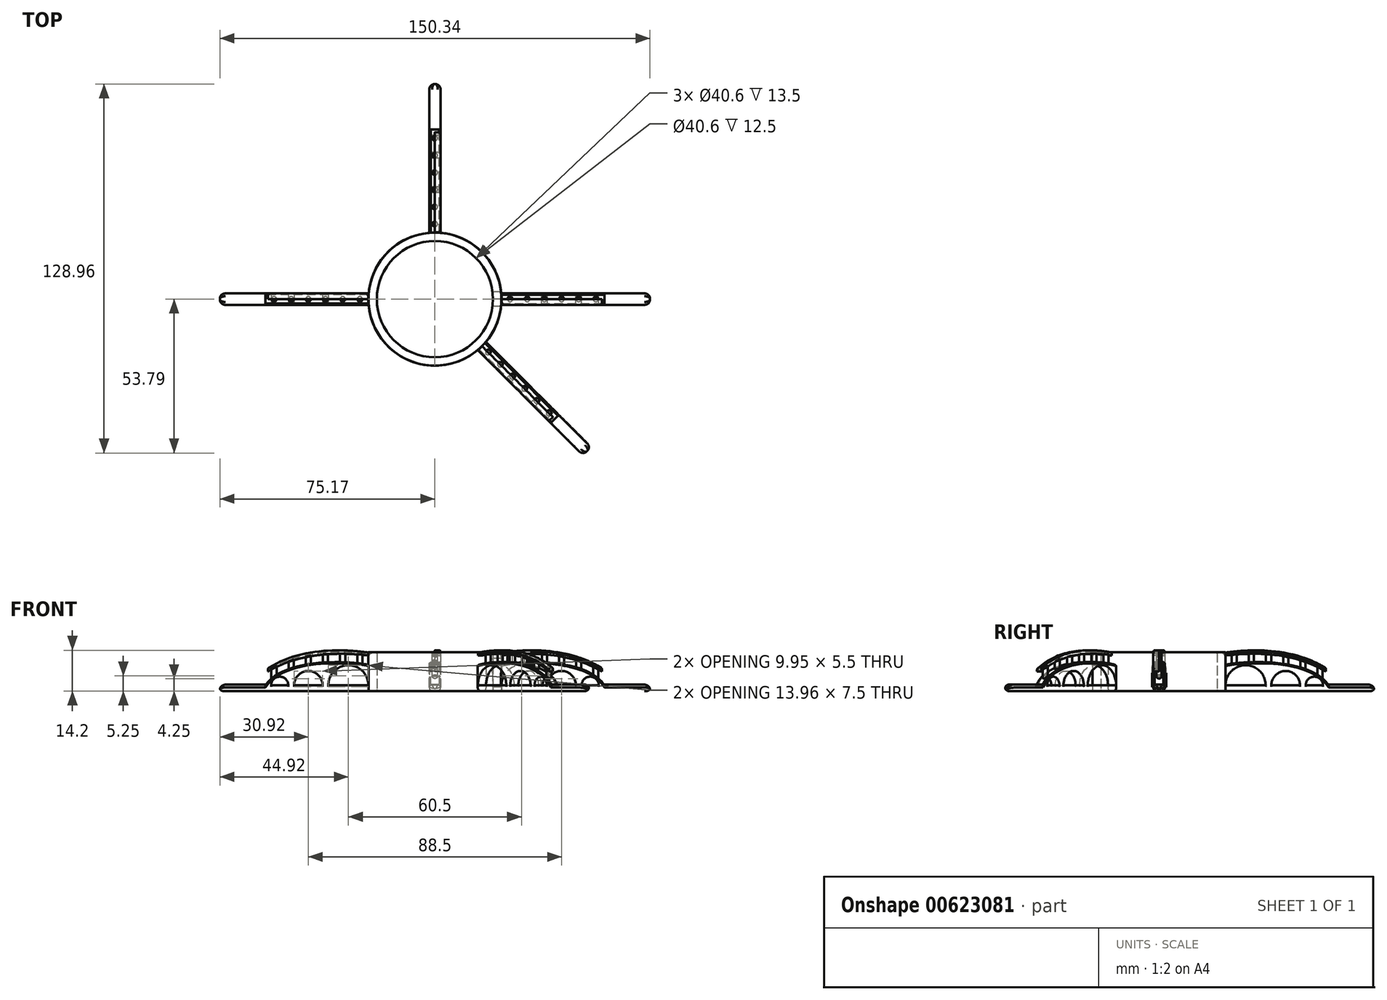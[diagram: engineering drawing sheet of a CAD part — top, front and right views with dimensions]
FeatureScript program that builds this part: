
annotation { "Feature Type Name" : "Feature", "Feature Type Description" : "" }
export const myFeature = defineFeature(function(context is Context, id is Id, definition is map)
    precondition{}
    {
        {
            var Q0;
            Q0=qCreatedBy(makeId("Top.planeOp"),FACE);
            var sketch = newSketch(context, id + "F0", { "sketchPlane" : qUnion([Q0])});
            skCircle(sketch, "E0", {"center": v(0, 0) * mm, "radius": 20.3 * mm});
            skCircle(sketch, "E1", {"center": v(0, 0) * mm, "radius": 23.25 * mm});
            skSolve(sketch);
        }
        {
            var Q0;
            Q0 = qSketchRegion(id + "F0", true);
            extrude(context, id + "F1", {"entities" : qUnion([Q0]), "depth" : 13.5 * mm, "offsetDistance" : 25 * mm});
        }
        {
            var Q0;
            Q0=qCreatedBy(makeId("Front.planeOp"),FACE);
            var sketch = newSketch(context, id + "F2", { "sketchPlane" : qUnion([Q0])});
            skLineSegment(sketch, "E2", {"start": v(0, 0) * mm, "end": v(23.25, 0) * mm});
            skLineSegment(sketch, "E3", {"start": v(23.25, 0) * mm, "end": v(23.25, 2) * mm});
            skLineSegment(sketch, "E4", {"start": v(23.25, 0) * mm, "end": v(16.87, 0) * mm});
            skLineSegment(sketch, "E5", {"start": v(59.25, 2) * mm, "end": v(23.25, 2) * mm});
            skPoint(sketch, "E6.start.orphan", {"position": v(16.87, 15) * mm});
            skLineSegment(sketch, "E7", {"start": v(23.25, 2) * mm, "end": v(23.25, 2) * mm});
            skLineSegment(sketch, "E8", {"start": v(23.25, 2) * mm, "end": v(23.25, 0) * mm});
            skLineSegment(sketch, "E9", {"start": v(23.25, 0) * mm, "end": v(23.25, 0) * mm});
            skLineSegment(sketch, "E10", {"start": v(23.25, 0) * mm, "end": v(59.25, 0) * mm});
            skArc(sketch, "E11", {"start": v(37.25, 2) * mm, "mid": v(30.25, 9) * mm, "end": v(23.25, 2) * mm});
            skLineSegment(sketch, "E12", {"start": v(37.25, 2) * mm, "end": v(39.25, 2) * mm});
            skLineSegment(sketch, "E13", {"start": v(39.25, 2) * mm, "end": v(39.25, 0) * mm});
            skArc(sketch, "E14", {"start": v(49.25, 2) * mm, "mid": v(44.25, 7) * mm, "end": v(39.25, 2) * mm});
            skLineSegment(sketch, "E15", {"start": v(49.25, 2) * mm, "end": v(51.25, 2) * mm});
            skLineSegment(sketch, "E16", {"start": v(51.25, 2) * mm, "end": v(51.25, 0) * mm});
            skArc(sketch, "E17", {"start": v(57.25, 2) * mm, "mid": v(54.25, 5) * mm, "end": v(51.25, 2) * mm});
            skLineSegment(sketch, "E18", {"start": v(57.25, 2) * mm, "end": v(59.25, 2) * mm});
            skLineSegment(sketch, "E19", {"start": v(23.25, 2) * mm, "end": v(21.25, 2) * mm});
            skLineSegment(sketch, "E20", {"start": v(21.25, 2) * mm, "end": v(21.25, 0) * mm});
            skLineSegment(sketch, "E21", {"start": v(59.25, 2) * mm, "end": v(59.25, 0) * mm});
            skFitSpline(sketch, "E22", {"points": [v(59.25, 2) * mm, v(22.94, 9.1) * mm], "startDerivative": vector(-19.37, 28.89) * mm, "endDerivative": vector(-21.33, -4.66) * mm});
            skLineSegment(sketch, "E23", {"start": v(22.94, 9.1) * mm, "end": v(21.25, 2) * mm});
            skLineSegment(sketch, "E24", {"start": v(59.25, 1.2) * mm, "end": v(59.25, 2) * mm});
            skSolve(sketch);
        }
        {
            var Q0;
            Q0 = qSketchRegion(id + "F2", true);
            extrude(context, id + "F3", {"entities" : qUnion([Q0]), "operationType" : NewBodyOperationType.ADD, "depth" : 4 * mm, "offsetDistance" : 25 * mm, "symmetric" : true});
        }
        {
            var Q0;
            Q0=makeQuery(id+"F1.opExtrude","CAP_FACE",FACE,{"disambiguationData":[OSD([sQuery(id+"F0.wireOp",EDGE,"E0"),sQuery(id+"F0.wireOp",EDGE,"E1")])],"isStart":false});
            var sketch = newSketch(context, id + "F4", { "sketchPlane" : qUnion([Q0])});
            skLineSegment(sketch, "E25", {"start": v(23.25, 0) * mm, "end": v(58.86, 0) * mm});
            skCircle(sketch, "E26", {"center": v(26.25, 0) * mm, "radius": 0.9 * mm});
            skLineSegment(sketch, "E27.direction1", {"start": v(26.25, 0) * mm, "end": v(32.25, 0) * mm, "construction": true});
            skCircle(sketch, "E28.1.0.0", {"center": v(32.25, 0) * mm, "radius": 0.9 * mm});
            skCircle(sketch, "E28.2.0.0", {"center": v(38.25, 0) * mm, "radius": 0.9 * mm});
            skCircle(sketch, "E28.3.0.0", {"center": v(44.25, 0) * mm, "radius": 0.9 * mm});
            skCircle(sketch, "E28.4.0.0", {"center": v(50.25, 0) * mm, "radius": 0.9 * mm});
            skCircle(sketch, "E28.5.0.0", {"center": v(56.25, 0) * mm, "radius": 0.9 * mm});
            skSolve(sketch);
        }
        {
            var Q0;
            Q0 = qSketchRegion(id + "F4", true);
            extrude(context, id + "F5", {"entities" : qUnion([Q0]), "operationType" : NewBodyOperationType.ADD, "endBound" : BoundingType.UP_TO_NEXT, "oppositeDirection" : true, "depth" : 25 * mm, "offsetDistance" : 25 * mm});
        }
        {
            var Q0;
            Q0=makeQuery(id+"F3.opExtrude","CAP_FACE",FACE,{"disambiguationData":[OSD([sQuery(id+"F2.wireOp",EDGE,"E4"),sQuery(id+"F2.wireOp",EDGE,"eUv9CqKa-Kuf0-0BP2-0XyY-XhsE2m74vfEs"),sQuery(id+"F2.wireOp",EDGE,"E5"),sQuery(id+"F2.wireOp",EDGE,"E10"),sQuery(id+"F2.wireOp",EDGE,"E11"),sQuery(id+"F2.wireOp",EDGE,"E14"),sQuery(id+"F2.wireOp",EDGE,"E17"),sQuery(id+"F2.wireOp",EDGE,"E5"),sQuery(id+"F2.wireOp",EDGE,"E20"),sQuery(id+"F2.wireOp",EDGE,"E22"),sQuery(id+"F2.wireOp",EDGE,"E23")])],"isStart":false});
            var sketch = newSketch(context, id + "F6", { "sketchPlane" : qUnion([Q0])});
            skFitSpline(sketch, "E29", {"points": [v(23.74, 12.54) * mm, v(61.85, 4.86) * mm], "startDerivative": vector(38.13, 4.2) * mm, "endDerivative": vector(33.52, -24.72) * mm});
            skLineSegment(sketch, "E30", {"start": v(23.74, 12.54) * mm, "end": v(23.74, 22.54) * mm});
            skLineSegment(sketch, "E31", {"start": v(61.85, 4.86) * mm, "end": v(61.85, 19.86) * mm});
            skFitSpline(sketch, "E32", {"points": [v(61.85, 19.86) * mm, v(23.74, 22.54) * mm], "startDerivative": vector(-32.68, 25.7) * mm, "endDerivative": vector(-38.13, -5.59) * mm});
            skSolve(sketch);
        }
        {
            var Q0;
            Q0 = qSketchRegion(id + "F6", true);
            extrude(context, id + "F7", {"entities" : qUnion([Q0]), "operationType" : NewBodyOperationType.REMOVE, "oppositeDirection" : true, "depth" : 7 * mm, "offsetDistance" : 25 * mm});
        }
        {
            var Q0;
            Q0=makeQuery(id+"F3.opExtrude","CAP_FACE",FACE,{"disambiguationData":[OSD([sQuery(id+"F2.wireOp",EDGE,"E4"),sQuery(id+"F2.wireOp",EDGE,"eUv9CqKa-Kuf0-0BP2-0XyY-XhsE2m74vfEs"),sQuery(id+"F2.wireOp",EDGE,"E5"),sQuery(id+"F2.wireOp",EDGE,"E10"),sQuery(id+"F2.wireOp",EDGE,"E11"),sQuery(id+"F2.wireOp",EDGE,"E14"),sQuery(id+"F2.wireOp",EDGE,"E17"),sQuery(id+"F2.wireOp",EDGE,"E5"),sQuery(id+"F2.wireOp",EDGE,"E20"),sQuery(id+"F2.wireOp",EDGE,"E22"),sQuery(id+"F2.wireOp",EDGE,"E23")])],"isStart":false});
            var sketch = newSketch(context, id + "F8", { "sketchPlane" : qUnion([Q0])});
            skFitSpline(sketch, "E33", {"points": [v(23.33, 12.44) * mm, v(61.44, 4.76) * mm], "startDerivative": vector(38.13, 4.2) * mm, "endDerivative": vector(33.52, -24.72) * mm});
            skLineSegment(sketch, "E34", {"start": v(23.33, 12.44) * mm, "end": v(23.33, 13.44) * mm});
            skFitSpline(sketch, "E35", {"points": [v(61.44, 5.76) * mm, v(23.33, 13.44) * mm], "startDerivative": vector(-33.52, 26.14) * mm, "endDerivative": vector(-38.16, -5.2) * mm});
            skLineSegment(sketch, "E36", {"start": v(58.3, 6.84) * mm, "end": v(58.3, 7.95) * mm});
            skSolve(sketch);
        }
        {
            var Q0;
            Q0 = qSketchRegion(id + "F8", true);
            extrude(context, id + "F9", {"entities" : qUnion([Q0]), "operationType" : NewBodyOperationType.ADD, "oppositeDirection" : true, "depth" : 2 * mm, "offsetDistance" : 25 * mm});
        }
        {
            var Q0;
            Q0=makeQuery(id+"F3.opExtrude","CAP_EDGE",EDGE,{"disambiguationData":[OSD([sQuery(id+"F2.wireOp",EDGE,"E22")])],"isStart":true});
            var Q1;
            Q1=makeQuery(id+"F3.opExtrude","CAP_EDGE",EDGE,{"disambiguationData":[OSD([sQuery(id+"F2.wireOp",EDGE,"E22")])],"isStart":false});
            chamfer(context, id + "F10", {"entities" : qUnion([Q0, Q1]), "chamferType" : ChamferType.OFFSET_ANGLE, "width" : 0.5 * mm, "oppositeDirection" : false, "angle" : 40 * degree, "tangentPropagation" : true});
        }
        {
            var Q0;
            {var subQ0=sQuery(id+"F2.wireOp",EDGE,"E5");var subQ1=sQuery(id+"F2.wireOp",EDGE,"E11");Q0=makeQuery(id+"F3.opExtrude","CAP_EDGE",EDGE,{"disambiguationData":[OSD([subQ0]),TDD([makeQuery(id+"F2.imprint","IMPRINT",EDGE,{"disambiguationData":[TD([[makeQuery(id+"F2.imprint","INTERSECT",VERTEX,{"derivedFrom":[subQ1,subQ0]}),-1.0]])],"derivedFrom":subQ0})])],"isStart":false});}
            var Q1;
            {var subQ0=sQuery(id+"F2.wireOp",EDGE,"E5");var subQ1=sQuery(id+"F2.wireOp",EDGE,"E14");Q1=makeQuery(id+"F3.opExtrude","CAP_EDGE",EDGE,{"disambiguationData":[OSD([subQ0]),TDD([makeQuery(id+"F2.imprint","IMPRINT",EDGE,{"disambiguationData":[TD([[makeQuery(id+"F2.imprint","INTERSECT",VERTEX,{"derivedFrom":[subQ1,subQ0]}),-1.0]])],"derivedFrom":subQ0})])],"isStart":false});}
            var Q2;
            {var subQ0=sQuery(id+"F2.wireOp",EDGE,"E5");var subQ1=sQuery(id+"F2.wireOp",EDGE,"E11");Q2=makeQuery(id+"F3.opExtrude","CAP_EDGE",EDGE,{"disambiguationData":[OSD([subQ0]),TDD([makeQuery(id+"F2.imprint","IMPRINT",EDGE,{"disambiguationData":[TD([[makeQuery(id+"F2.imprint","INTERSECT",VERTEX,{"derivedFrom":[subQ1,subQ0]}),-1.0]])],"derivedFrom":subQ0})])],"isStart":true});}
            var Q3;
            {var subQ0=sQuery(id+"F2.wireOp",EDGE,"E5");var subQ1=sQuery(id+"F2.wireOp",EDGE,"E14");Q3=makeQuery(id+"F3.opExtrude","CAP_EDGE",EDGE,{"disambiguationData":[OSD([subQ0]),TDD([makeQuery(id+"F2.imprint","IMPRINT",EDGE,{"disambiguationData":[TD([[makeQuery(id+"F2.imprint","INTERSECT",VERTEX,{"derivedFrom":[subQ1,subQ0]}),-1.0]])],"derivedFrom":subQ0})])],"isStart":true});}
            var Q4;
            {var subQ0=sQuery(id+"F2.wireOp",EDGE,"E5");var subQ1=sQuery(id+"F2.wireOp",EDGE,"E17");Q4=makeQuery(id+"F3.opExtrude","CAP_EDGE",EDGE,{"disambiguationData":[OSD([subQ0]),TDD([makeQuery(id+"F2.imprint","IMPRINT",EDGE,{"disambiguationData":[TD([[makeQuery(id+"F2.imprint","INTERSECT",VERTEX,{"derivedFrom":[subQ1,subQ0]}),-1.0]])],"derivedFrom":subQ0})])],"isStart":true});}
            var Q5;
            {var subQ0=sQuery(id+"F2.wireOp",EDGE,"E5");var subQ1=sQuery(id+"F2.wireOp",EDGE,"E17");Q5=makeQuery(id+"F3.opExtrude","CAP_EDGE",EDGE,{"disambiguationData":[OSD([subQ0]),TDD([makeQuery(id+"F2.imprint","IMPRINT",EDGE,{"disambiguationData":[TD([[makeQuery(id+"F2.imprint","INTERSECT",VERTEX,{"derivedFrom":[subQ1,subQ0]}),-1.0]])],"derivedFrom":subQ0})])],"isStart":false});}
            var Q6;
            Q6=makeQuery(id+"FbmkzwlNqpSPATz_1.1.F9.opExtrude","CAP_EDGE",EDGE,{"disambiguationData":[OSD([sQuery(id+"F8.wireOp",EDGE,"E35")])],"isStart":true});
            var Q7;
            Q7=makeQuery(id+"F9.opExtrude","CAP_EDGE",EDGE,{"disambiguationData":[OSD([sQuery(id+"F8.wireOp",EDGE,"E35")])],"isStart":true});
            var Q8;
            {var subQ0=sQuery(id+"F8.wireOp",EDGE,"E35");var subQ1=sQuery(id+"F8.wireOp",EDGE,"bGR884Nu-NAzO-R1rn-mJv8-BLiTySfXEnIB");Q8=makeQuery(id+"FbmkzwlNqpSPATz_1.1.F9.boolean.opBoolean","MERGE",EDGE,{"derivedFrom":[makeQuery(id+"F9.opExtrude","SWEPT_EDGE",EDGE,{"disambiguationData":[OSD([subQ1,subQ0])]}),makeQuery(id+"FbmkzwlNqpSPATz_1.1.F9.opExtrude","SWEPT_EDGE",EDGE,{"disambiguationData":[OSD([subQ1,subQ0])]})]});}
            fillet(context, id + "F11", {"entities" : qUnion([Q0, Q1, Q2, Q3, Q4, Q5, Q6, Q7, Q8]), "radius" : 0.5 * mm, "tangentPropagation" : true, "allowEdgeOverflow" : false});
        }
        {
            var Q0;
            Q0=makeQuery(id+"F3.opExtrude","CAP_FACE",FACE,{"disambiguationData":[OSD([sQuery(id+"F2.wireOp",EDGE,"E4"),sQuery(id+"F2.wireOp",EDGE,"E10"),sQuery(id+"F2.wireOp",EDGE,"E11"),sQuery(id+"F2.wireOp",EDGE,"E14"),sQuery(id+"F2.wireOp",EDGE,"E17"),sQuery(id+"F2.wireOp",EDGE,"E5"),sQuery(id+"F2.wireOp",EDGE,"E20"),sQuery(id+"F2.wireOp",EDGE,"E21"),sQuery(id+"F2.wireOp",EDGE,"E22"),sQuery(id+"F2.wireOp",EDGE,"E23"),sQuery(id+"F2.wireOp",EDGE,"E24")])],"isStart":true});
            var sketch = newSketch(context, id + "F12", { "sketchPlane" : qUnion([Q0])});
            skLineSegment(sketch, "E37", {"start": v(-59.25, 0) * mm, "end": v(-75.25, 0) * mm});
            skLineSegment(sketch, "E38", {"start": v(-75.25, 0) * mm, "end": v(-75.25, 2.2) * mm});
            skLineSegment(sketch, "E39", {"start": v(-75.25, 2.2) * mm, "end": v(-59.25, 2.2) * mm});
            skLineSegment(sketch, "E40", {"start": v(-59.25, 2.2) * mm, "end": v(-59.25, 0) * mm});
            skSolve(sketch);
        }
        {
            var Q0;
            Q0 = qSketchRegion(id + "F12", true);
            extrude(context, id + "F13", {"entities" : qUnion([Q0]), "operationType" : NewBodyOperationType.ADD, "oppositeDirection" : true, "depth" : 4 * mm, "offsetDistance" : 25 * mm});
        }
        {
            var Q0;
            Q0=makeQuery(id+"F13.opExtrude","CAP_EDGE",EDGE,{"disambiguationData":[OSD([sQuery(id+"F12.wireOp",EDGE,"E39")])],"isStart":true});
            var Q1;
            Q1=makeQuery(id+"F13.opExtrude","CAP_EDGE",EDGE,{"disambiguationData":[OSD([sQuery(id+"F12.wireOp",EDGE,"E39")])],"isStart":false});
            fillet(context, id + "F14", {"entities" : qUnion([Q0, Q1]), "radius" : 1 * mm, "tangentPropagation" : true, "allowEdgeOverflow" : false});
        }
        {
            var Q0;
            Q0=makeQuery(id+"F14.opFillet","BLEND_EDGE",EDGE,{"blendedFrom":[makeQuery(id+"F13.opExtrude","CAP_EDGE",EDGE,{"disambiguationData":[OSD([sQuery(id+"F12.wireOp",EDGE,"E39")])],"isStart":true}),makeQuery(id+"F13.opExtrude","SWEPT_FACE",FACE,{"disambiguationData":[OSD([sQuery(id+"F12.wireOp",EDGE,"E38")])]})],"blendedInto":[makeQuery(id+"F13.opExtrude","SWEPT_FACE",FACE,{"disambiguationData":[OSD([sQuery(id+"F12.wireOp",EDGE,"E38")])]})]});
            fillet(context, id + "F15", {"entities" : qUnion([Q0]), "radius" : 2 * mm, "tangentPropagation" : true, "allowEdgeOverflow" : false});
        }
        {
            var Q0;
            Q0=makeQuery(id+"F1.opExtrude","SWEPT_BODY",BODY,{"disambiguationData":[OSD([sQuery(id+"F0.wireOp",EDGE,"E0"),sQuery(id+"F0.wireOp",EDGE,"E1")])]});
            var Q1;
            Q1=makeQuery(id+"F1.opExtrude","CAP_EDGE",EDGE,{"disambiguationData":[OSD([sQuery(id+"F0.wireOp",EDGE,"E1")])],"isStart":false});
            circularPattern(context, id + "F16", {"entities" : qUnion([Q0]), "axis" : qUnion([Q1]), "angle" : 360 * degree, "instanceCount" : 4, "equalSpace" : true});
        }
        {
            var Q0;
            Q0=qCreatedBy(makeId("Right.planeOp"),FACE);
            var sketch = newSketch(context, id + "F17", { "sketchPlane" : qUnion([Q0])});
            skLineSegment(sketch, "E41.bottom", {"start": v(2.5, 6.34) * mm, "end": v(-2.5, 6.34) * mm});
            skLineSegment(sketch, "E41.top", {"start": v(2.5, 1.34) * mm, "end": v(-2.5, 1.34) * mm});
            skLineSegment(sketch, "E41.left", {"start": v(2.5, 6.34) * mm, "end": v(2.5, 1.34) * mm});
            skLineSegment(sketch, "E41.right", {"start": v(-2.5, 6.34) * mm, "end": v(-2.5, 1.34) * mm});
            skPoint(sketch, "E41.middle", {"position": v(0, 3.84) * mm});
            skPoint(sketch, "E42.1.internal.snap0", {"position": v(0, 6.34) * mm});
            skFitSpline(sketch, "E42", {"points": [v(-2.5, 6.34) * mm, v(0, 11.34) * mm], "startDerivative": vector(0, 6.14) * mm, "endDerivative": vector(7.5, 3.82) * mm});
            skFitSpline(sketch, "E43", {"points": [v(2.5, 6.34) * mm, v(0, 11.34) * mm], "startDerivative": vector(0, 6.14) * mm, "endDerivative": vector(-7.5, 3.82) * mm});
            skSolve(sketch);
        }
        {
            var Q0;
            Q0=makeQuery(id+"F17.imprint","IMPRINT",FACE,{"disambiguationData":[TD([[makeQuery(id+"F17.imprint","IMPRINT",EDGE,{"derivedFrom":sQuery(id+"F17.wireOp",EDGE,"E41.bottom")}),1.0]])]});
            var Q1;
            Q1=makeQuery(id+"F17.imprint","IMPRINT",FACE,{"disambiguationData":[TD([[makeQuery(id+"F17.imprint","IMPRINT",EDGE,{"derivedFrom":sQuery(id+"F17.wireOp",EDGE,"E41.bottom")}),-1.0]])]});
            var Q2;
            Q2=makeQuery(id+"F16.opPattern","COPY",FACE,{"derivedFrom":makeQuery(id+"F1.opExtrude","SWEPT_FACE",FACE,{"disambiguationData":[OSD([sQuery(id+"F0.wireOp",EDGE,"E1")])]}),"instanceName":"1"});
            extrude(context, id + "F18", {"entities" : qUnion([Q0, Q1]), "depth" : 25 * mm, "endBoundEntityFace" : qUnion([Q2]), "offsetDistance" : 25 * mm});
        }
        {
            var Q0;
            Q0=makeQuery(id+"F16.opPattern","COPY",BODY,{"derivedFrom":makeQuery(id+"F1.opExtrude","SWEPT_BODY",BODY,{"disambiguationData":[OSD([sQuery(id+"F0.wireOp",EDGE,"E0"),sQuery(id+"F0.wireOp",EDGE,"E1")])]}),"instanceName":"3"});
            var Q1;
            Q1=makeQuery(id+"F16.opPattern","COPY",EDGE,{"derivedFrom":makeQuery(id+"F1.opExtrude","CAP_EDGE",EDGE,{"disambiguationData":[OSD([sQuery(id+"F0.wireOp",EDGE,"E1")])],"isStart":false}),"instanceName":"3"});
            transform(context, id + "F19", {"entities" : qUnion([Q0]), "transformType" : TransformType.ROTATION, "transformAxis" : qUnion([Q1]), "angle" : 45 * degree, "makeCopy" : false});
        }
        {
            var Q0;
            Q0=makeQuery(id+"F18.opExtrude","SWEPT_BODY",BODY,{"disambiguationData":[OSD([sQuery(id+"F17.wireOp",EDGE,"E41.top"),sQuery(id+"F17.wireOp",EDGE,"E41.left"),sQuery(id+"F17.wireOp",EDGE,"E41.right"),sQuery(id+"F17.wireOp",EDGE,"E42"),sQuery(id+"F17.wireOp",EDGE,"E43")])]});
            var Q1;
            Q1=makeQuery(id+"FSJmOjyLK6ZuT0z_1.-11.F18.opExtrude","SWEPT_BODY",BODY,{"disambiguationData":[OSD([sQuery(id+"F17.wireOp",EDGE,"E41.top"),sQuery(id+"F17.wireOp",EDGE,"E41.left"),sQuery(id+"F17.wireOp",EDGE,"E41.right"),sQuery(id+"F17.wireOp",EDGE,"E42"),sQuery(id+"F17.wireOp",EDGE,"E43")])]});
            var Q2;
            Q2=makeQuery(id+"FSJmOjyLK6ZuT0z_1.-10.F18.opExtrude","SWEPT_BODY",BODY,{"disambiguationData":[OSD([sQuery(id+"F17.wireOp",EDGE,"E41.top"),sQuery(id+"F17.wireOp",EDGE,"E41.left"),sQuery(id+"F17.wireOp",EDGE,"E41.right"),sQuery(id+"F17.wireOp",EDGE,"E42"),sQuery(id+"F17.wireOp",EDGE,"E43")])]});
            var Q3;
            Q3=makeQuery(id+"FSJmOjyLK6ZuT0z_1.-9.F18.opExtrude","SWEPT_BODY",BODY,{"disambiguationData":[OSD([sQuery(id+"F17.wireOp",EDGE,"E41.top"),sQuery(id+"F17.wireOp",EDGE,"E41.left"),sQuery(id+"F17.wireOp",EDGE,"E41.right"),sQuery(id+"F17.wireOp",EDGE,"E42"),sQuery(id+"F17.wireOp",EDGE,"E43")])]});
            var Q4;
            Q4=makeQuery(id+"FSJmOjyLK6ZuT0z_1.-8.F18.opExtrude","SWEPT_BODY",BODY,{"disambiguationData":[OSD([sQuery(id+"F17.wireOp",EDGE,"E41.top"),sQuery(id+"F17.wireOp",EDGE,"E41.left"),sQuery(id+"F17.wireOp",EDGE,"E41.right"),sQuery(id+"F17.wireOp",EDGE,"E42"),sQuery(id+"F17.wireOp",EDGE,"E43")])]});
            var Q5;
            Q5=makeQuery(id+"FSJmOjyLK6ZuT0z_1.-7.F18.opExtrude","SWEPT_BODY",BODY,{"disambiguationData":[OSD([sQuery(id+"F17.wireOp",EDGE,"E41.top"),sQuery(id+"F17.wireOp",EDGE,"E41.left"),sQuery(id+"F17.wireOp",EDGE,"E41.right"),sQuery(id+"F17.wireOp",EDGE,"E42"),sQuery(id+"F17.wireOp",EDGE,"E43")])]});
            var Q6;
            Q6=makeQuery(id+"FSJmOjyLK6ZuT0z_1.-6.F18.opExtrude","SWEPT_BODY",BODY,{"disambiguationData":[OSD([sQuery(id+"F17.wireOp",EDGE,"E41.top"),sQuery(id+"F17.wireOp",EDGE,"E41.left"),sQuery(id+"F17.wireOp",EDGE,"E41.right"),sQuery(id+"F17.wireOp",EDGE,"E42"),sQuery(id+"F17.wireOp",EDGE,"E43")])]});
            var Q7;
            Q7=makeQuery(id+"FSJmOjyLK6ZuT0z_1.-5.F18.opExtrude","SWEPT_BODY",BODY,{"disambiguationData":[OSD([sQuery(id+"F17.wireOp",EDGE,"E41.top"),sQuery(id+"F17.wireOp",EDGE,"E41.left"),sQuery(id+"F17.wireOp",EDGE,"E41.right"),sQuery(id+"F17.wireOp",EDGE,"E42"),sQuery(id+"F17.wireOp",EDGE,"E43")])]});
            var Q8;
            Q8=makeQuery(id+"FSJmOjyLK6ZuT0z_1.-4.F18.opExtrude","SWEPT_BODY",BODY,{"disambiguationData":[OSD([sQuery(id+"F17.wireOp",EDGE,"E41.top"),sQuery(id+"F17.wireOp",EDGE,"E41.left"),sQuery(id+"F17.wireOp",EDGE,"E41.right"),sQuery(id+"F17.wireOp",EDGE,"E42"),sQuery(id+"F17.wireOp",EDGE,"E43")])]});
            var Q9;
            Q9=makeQuery(id+"FSJmOjyLK6ZuT0z_1.-3.F18.opExtrude","SWEPT_BODY",BODY,{"disambiguationData":[OSD([sQuery(id+"F17.wireOp",EDGE,"E41.top"),sQuery(id+"F17.wireOp",EDGE,"E41.left"),sQuery(id+"F17.wireOp",EDGE,"E41.right"),sQuery(id+"F17.wireOp",EDGE,"E42"),sQuery(id+"F17.wireOp",EDGE,"E43")])]});
            var Q10;
            Q10=makeQuery(id+"FSJmOjyLK6ZuT0z_1.-2.F18.opExtrude","SWEPT_BODY",BODY,{"disambiguationData":[OSD([sQuery(id+"F17.wireOp",EDGE,"E41.top"),sQuery(id+"F17.wireOp",EDGE,"E41.left"),sQuery(id+"F17.wireOp",EDGE,"E41.right"),sQuery(id+"F17.wireOp",EDGE,"E42"),sQuery(id+"F17.wireOp",EDGE,"E43")])]});
            var Q11;
            Q11=makeQuery(id+"FSJmOjyLK6ZuT0z_1.-1.F18.opExtrude","SWEPT_BODY",BODY,{"disambiguationData":[OSD([sQuery(id+"F17.wireOp",EDGE,"E41.top"),sQuery(id+"F17.wireOp",EDGE,"E41.left"),sQuery(id+"F17.wireOp",EDGE,"E41.right"),sQuery(id+"F17.wireOp",EDGE,"E42"),sQuery(id+"F17.wireOp",EDGE,"E43")])]});
            var Q12;
            Q12=makeQuery(id+"FSJmOjyLK6ZuT0z_1.1.F18.opExtrude","SWEPT_BODY",BODY,{"disambiguationData":[OSD([sQuery(id+"F17.wireOp",EDGE,"E41.top"),sQuery(id+"F17.wireOp",EDGE,"E41.left"),sQuery(id+"F17.wireOp",EDGE,"E41.right"),sQuery(id+"F17.wireOp",EDGE,"E42"),sQuery(id+"F17.wireOp",EDGE,"E43")])]});
            var Q13;
            Q13=makeQuery(id+"FSJmOjyLK6ZuT0z_1.2.F18.opExtrude","SWEPT_BODY",BODY,{"disambiguationData":[OSD([sQuery(id+"F17.wireOp",EDGE,"E41.top"),sQuery(id+"F17.wireOp",EDGE,"E41.left"),sQuery(id+"F17.wireOp",EDGE,"E41.right"),sQuery(id+"F17.wireOp",EDGE,"E42"),sQuery(id+"F17.wireOp",EDGE,"E43")])]});
            var Q14;
            Q14=makeQuery(id+"FSJmOjyLK6ZuT0z_1.3.F18.opExtrude","SWEPT_BODY",BODY,{"disambiguationData":[OSD([sQuery(id+"F17.wireOp",EDGE,"E41.top"),sQuery(id+"F17.wireOp",EDGE,"E41.left"),sQuery(id+"F17.wireOp",EDGE,"E41.right"),sQuery(id+"F17.wireOp",EDGE,"E42"),sQuery(id+"F17.wireOp",EDGE,"E43")])]});
            var Q15;
            Q15=makeQuery(id+"FSJmOjyLK6ZuT0z_1.4.F18.opExtrude","SWEPT_BODY",BODY,{"disambiguationData":[OSD([sQuery(id+"F17.wireOp",EDGE,"E41.top"),sQuery(id+"F17.wireOp",EDGE,"E41.left"),sQuery(id+"F17.wireOp",EDGE,"E41.right"),sQuery(id+"F17.wireOp",EDGE,"E42"),sQuery(id+"F17.wireOp",EDGE,"E43")])]});
            var Q16;
            Q16=makeQuery(id+"FSJmOjyLK6ZuT0z_1.5.F18.opExtrude","SWEPT_BODY",BODY,{"disambiguationData":[OSD([sQuery(id+"F17.wireOp",EDGE,"E41.top"),sQuery(id+"F17.wireOp",EDGE,"E41.left"),sQuery(id+"F17.wireOp",EDGE,"E41.right"),sQuery(id+"F17.wireOp",EDGE,"E42"),sQuery(id+"F17.wireOp",EDGE,"E43")])]});
            var Q17;
            Q17=makeQuery(id+"FSJmOjyLK6ZuT0z_1.6.F18.opExtrude","SWEPT_BODY",BODY,{"disambiguationData":[OSD([sQuery(id+"F17.wireOp",EDGE,"E41.top"),sQuery(id+"F17.wireOp",EDGE,"E41.left"),sQuery(id+"F17.wireOp",EDGE,"E41.right"),sQuery(id+"F17.wireOp",EDGE,"E42"),sQuery(id+"F17.wireOp",EDGE,"E43")])]});
            var Q18;
            Q18=makeQuery(id+"FSJmOjyLK6ZuT0z_1.7.F18.opExtrude","SWEPT_BODY",BODY,{"disambiguationData":[OSD([sQuery(id+"F17.wireOp",EDGE,"E41.top"),sQuery(id+"F17.wireOp",EDGE,"E41.left"),sQuery(id+"F17.wireOp",EDGE,"E41.right"),sQuery(id+"F17.wireOp",EDGE,"E42"),sQuery(id+"F17.wireOp",EDGE,"E43")])]});
            var Q19;
            Q19=makeQuery(id+"FSJmOjyLK6ZuT0z_1.8.F18.opExtrude","SWEPT_BODY",BODY,{"disambiguationData":[OSD([sQuery(id+"F17.wireOp",EDGE,"E41.top"),sQuery(id+"F17.wireOp",EDGE,"E41.left"),sQuery(id+"F17.wireOp",EDGE,"E41.right"),sQuery(id+"F17.wireOp",EDGE,"E42"),sQuery(id+"F17.wireOp",EDGE,"E43")])]});
            var Q20;
            Q20=makeQuery(id+"FSJmOjyLK6ZuT0z_1.9.F18.opExtrude","SWEPT_BODY",BODY,{"disambiguationData":[OSD([sQuery(id+"F17.wireOp",EDGE,"E41.top"),sQuery(id+"F17.wireOp",EDGE,"E41.left"),sQuery(id+"F17.wireOp",EDGE,"E41.right"),sQuery(id+"F17.wireOp",EDGE,"E42"),sQuery(id+"F17.wireOp",EDGE,"E43")])]});
            var Q21;
            Q21=makeQuery(id+"FSJmOjyLK6ZuT0z_1.10.F18.opExtrude","SWEPT_BODY",BODY,{"disambiguationData":[OSD([sQuery(id+"F17.wireOp",EDGE,"E41.top"),sQuery(id+"F17.wireOp",EDGE,"E41.left"),sQuery(id+"F17.wireOp",EDGE,"E41.right"),sQuery(id+"F17.wireOp",EDGE,"E42"),sQuery(id+"F17.wireOp",EDGE,"E43")])]});
            var Q22;
            Q22=makeQuery(id+"FSJmOjyLK6ZuT0z_1.11.F18.opExtrude","SWEPT_BODY",BODY,{"disambiguationData":[OSD([sQuery(id+"F17.wireOp",EDGE,"E41.top"),sQuery(id+"F17.wireOp",EDGE,"E41.left"),sQuery(id+"F17.wireOp",EDGE,"E41.right"),sQuery(id+"F17.wireOp",EDGE,"E42"),sQuery(id+"F17.wireOp",EDGE,"E43")])]});
            var Q23;
            Q23=makeQuery(id+"F16.opPattern","COPY",BODY,{"derivedFrom":makeQuery(id+"F1.opExtrude","SWEPT_BODY",BODY,{"disambiguationData":[OSD([sQuery(id+"F0.wireOp",EDGE,"E0"),sQuery(id+"F0.wireOp",EDGE,"E1")])]}),"instanceName":"3"});
            booleanBodies(context, id + "F20", {"operationType" : BooleanOperationType.SUBTRACTION, "tools" : qUnion([Q0, Q1, Q2, Q3, Q4, Q5, Q6, Q7, Q8, Q9, Q10, Q11, Q12, Q13, Q14, Q15, Q16, Q17, Q18, Q19, Q20, Q21, Q22]), "targets" : qUnion([Q23])});
        }
        {
            var Q0;
            Q0=makeQuery(id+"F16.opPattern","COPY",EDGE,{"derivedFrom":makeQuery(id+"F1.opExtrude","CAP_EDGE",EDGE,{"disambiguationData":[OSD([sQuery(id+"F0.wireOp",EDGE,"E1")])],"isStart":false}),"instanceName":"3"});
            fillet(context, id + "F21", {"entities" : qUnion([Q0]), "radius" : 2 * mm, "tangentPropagation" : true, "allowEdgeOverflow" : false});
        }
        {
            var Q0;
            Q0=makeQuery(id+"F16.opPattern","COPY",EDGE,{"derivedFrom":makeQuery(id+"F1.opExtrude","CAP_EDGE",EDGE,{"disambiguationData":[OSD([sQuery(id+"F0.wireOp",EDGE,"E0")])],"isStart":false}),"instanceName":"3"});
            var Q1;
            Q1=makeQuery(id+"F16.opPattern","COPY",EDGE,{"derivedFrom":makeQuery(id+"F1.opExtrude","CAP_EDGE",EDGE,{"disambiguationData":[OSD([sQuery(id+"F0.wireOp",EDGE,"E0")])],"isStart":true}),"instanceName":"3"});
            fillet(context, id + "F22", {"entities" : qUnion([Q0, Q1]), "radius" : 0.5 * mm, "tangentPropagation" : true, "allowEdgeOverflow" : false});
        }
        {
            var Q0;
            Q0=makeQuery(id+"F16.opPattern","COPY",EDGE,{"derivedFrom":makeQuery(id+"F13.boolean.opBoolean","MERGE",EDGE,{"derivedFrom":[makeQuery(id+"F3.opExtrude","CAP_EDGE",EDGE,{"disambiguationData":[OSD([sQuery(id+"F2.wireOp",EDGE,"E4"),sQuery(id+"F2.wireOp",EDGE,"E10")])],"isStart":false}),makeQuery(id+"F13.opExtrude","CAP_EDGE",EDGE,{"disambiguationData":[OSD([sQuery(id+"F12.wireOp",EDGE,"E37")])],"isStart":false})]}),"instanceName":"1"});
            var Q1;
            Q1=makeQuery(id+"F16.opPattern","COPY",EDGE,{"derivedFrom":makeQuery(id+"F13.boolean.opBoolean","MERGE",EDGE,{"derivedFrom":[makeQuery(id+"F3.opExtrude","CAP_EDGE",EDGE,{"disambiguationData":[OSD([sQuery(id+"F2.wireOp",EDGE,"E4"),sQuery(id+"F2.wireOp",EDGE,"E10")])],"isStart":true}),makeQuery(id+"F13.opExtrude","CAP_EDGE",EDGE,{"disambiguationData":[OSD([sQuery(id+"F12.wireOp",EDGE,"E37")])],"isStart":true})]}),"instanceName":"1"});
            var Q2;
            Q2=makeQuery(id+"F16.opPattern","COPY",EDGE,{"derivedFrom":makeQuery(id+"F13.boolean.opBoolean","MERGE",EDGE,{"derivedFrom":[makeQuery(id+"F3.opExtrude","CAP_EDGE",EDGE,{"disambiguationData":[OSD([sQuery(id+"F2.wireOp",EDGE,"E4"),sQuery(id+"F2.wireOp",EDGE,"E10")])],"isStart":false}),makeQuery(id+"F13.opExtrude","CAP_EDGE",EDGE,{"disambiguationData":[OSD([sQuery(id+"F12.wireOp",EDGE,"E37")])],"isStart":false})]}),"instanceName":"2"});
            var Q3;
            Q3=makeQuery(id+"F16.opPattern","COPY",EDGE,{"derivedFrom":makeQuery(id+"F13.boolean.opBoolean","MERGE",EDGE,{"derivedFrom":[makeQuery(id+"F3.opExtrude","CAP_EDGE",EDGE,{"disambiguationData":[OSD([sQuery(id+"F2.wireOp",EDGE,"E4"),sQuery(id+"F2.wireOp",EDGE,"E10")])],"isStart":true}),makeQuery(id+"F13.opExtrude","CAP_EDGE",EDGE,{"disambiguationData":[OSD([sQuery(id+"F12.wireOp",EDGE,"E37")])],"isStart":true})]}),"instanceName":"2"});
            var Q4;
            Q4=makeQuery(id+"F16.opPattern","COPY",EDGE,{"derivedFrom":makeQuery(id+"F13.boolean.opBoolean","MERGE",EDGE,{"derivedFrom":[makeQuery(id+"F3.opExtrude","CAP_EDGE",EDGE,{"disambiguationData":[OSD([sQuery(id+"F2.wireOp",EDGE,"E4"),sQuery(id+"F2.wireOp",EDGE,"E10")])],"isStart":false}),makeQuery(id+"F13.opExtrude","CAP_EDGE",EDGE,{"disambiguationData":[OSD([sQuery(id+"F12.wireOp",EDGE,"E37")])],"isStart":false})]}),"instanceName":"3"});
            var Q5;
            Q5=makeQuery(id+"F16.opPattern","COPY",EDGE,{"derivedFrom":makeQuery(id+"F13.boolean.opBoolean","MERGE",EDGE,{"derivedFrom":[makeQuery(id+"F3.opExtrude","CAP_EDGE",EDGE,{"disambiguationData":[OSD([sQuery(id+"F2.wireOp",EDGE,"E4"),sQuery(id+"F2.wireOp",EDGE,"E10")])],"isStart":true}),makeQuery(id+"F13.opExtrude","CAP_EDGE",EDGE,{"disambiguationData":[OSD([sQuery(id+"F12.wireOp",EDGE,"E37")])],"isStart":true})]}),"instanceName":"3"});
            var Q6;
            Q6=makeQuery(id+"F13.boolean.opBoolean","MERGE",EDGE,{"derivedFrom":[makeQuery(id+"F3.opExtrude","CAP_EDGE",EDGE,{"disambiguationData":[OSD([sQuery(id+"F2.wireOp",EDGE,"E4"),sQuery(id+"F2.wireOp",EDGE,"E10")])],"isStart":true}),makeQuery(id+"F13.opExtrude","CAP_EDGE",EDGE,{"disambiguationData":[OSD([sQuery(id+"F12.wireOp",EDGE,"E37")])],"isStart":true})]});
            var Q7;
            Q7=makeQuery(id+"F13.boolean.opBoolean","MERGE",EDGE,{"derivedFrom":[makeQuery(id+"F3.opExtrude","CAP_EDGE",EDGE,{"disambiguationData":[OSD([sQuery(id+"F2.wireOp",EDGE,"E4"),sQuery(id+"F2.wireOp",EDGE,"E10")])],"isStart":false}),makeQuery(id+"F13.opExtrude","CAP_EDGE",EDGE,{"disambiguationData":[OSD([sQuery(id+"F12.wireOp",EDGE,"E37")])],"isStart":false})]});
            fillet(context, id + "F23", {"entities" : qUnion([Q0, Q1, Q2, Q3, Q4, Q5, Q6, Q7]), "radius" : 1.2 * mm, "tangentPropagation" : true, "allowEdgeOverflow" : false});
        }
    });
